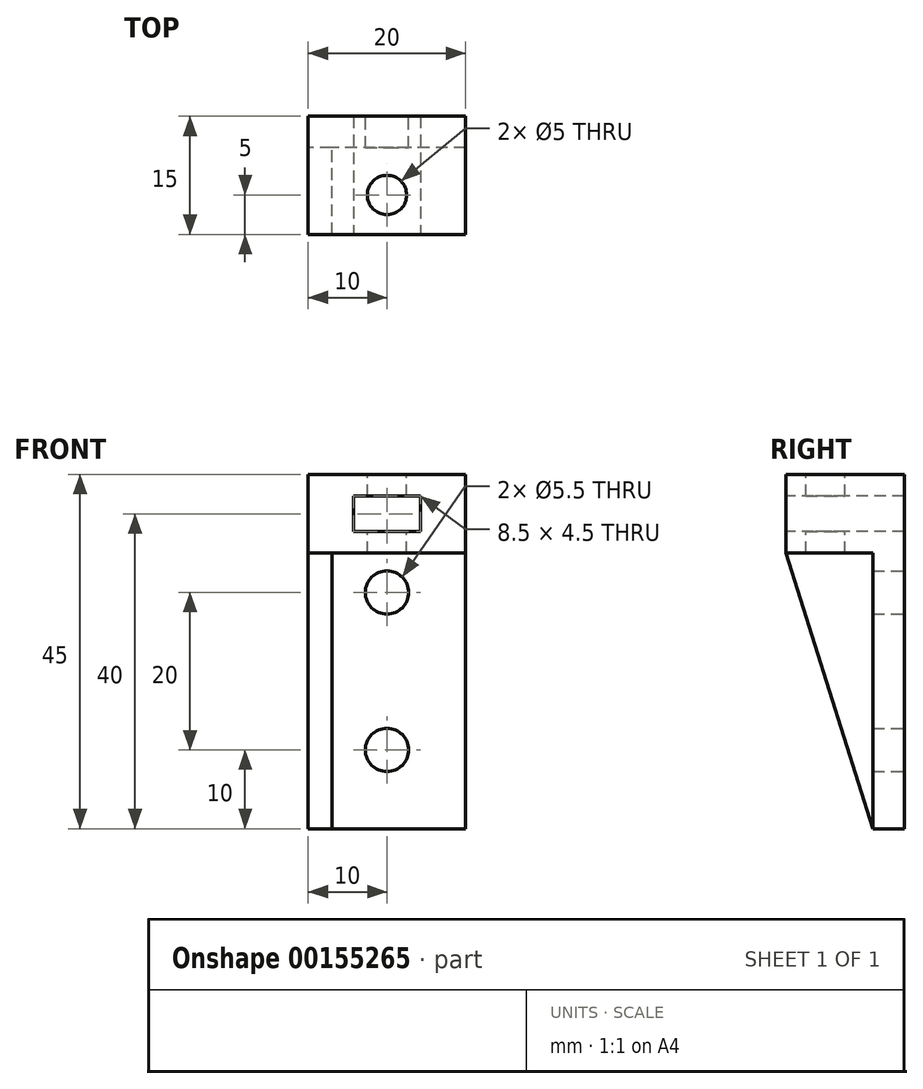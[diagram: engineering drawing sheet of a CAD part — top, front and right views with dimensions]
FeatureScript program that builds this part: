
annotation { "Feature Type Name" : "Feature", "Feature Type Description" : "" }
export const myFeature = defineFeature(function(context is Context, id is Id, definition is map)
    precondition{}
    {
        {
            var Q0;
            Q0=qCreatedBy(makeId("Front.planeOp"),FACE);
            var sketch = newSketch(context, id + "F0", { "sketchPlane" : qUnion([Q0])});
            skCircle(sketch, "E0", {"center": v(0, 10) * mm, "radius": 2.75 * mm});
            skCircle(sketch, "E1", {"center": v(0, -10) * mm, "radius": 2.75 * mm});
            skLineSegment(sketch, "E2.bottom", {"start": v(10, -20) * mm, "end": v(-10, -20) * mm});
            skLineSegment(sketch, "E2.top", {"start": v(10, 20) * mm, "end": v(-10, 20) * mm});
            skLineSegment(sketch, "E2.left", {"start": v(10, -20) * mm, "end": v(10, 20) * mm});
            skLineSegment(sketch, "E2.right", {"start": v(-10, -20) * mm, "end": v(-10, 20) * mm});
            skPoint(sketch, "E2.middle", {"position": v(0, 0) * mm});
            skSolve(sketch);
        }
        {
            var Q0;
            Q0 = qSketchRegion(id + "F0", true);
            extrude(context, id + "F1", {"entities" : qUnion([Q0]), "depth" : 4 * mm});
        }
        {
            var Q0;
            Q0=makeQuery(id+"F1.opExtrude","CAP_FACE",FACE,{"disambiguationData":[OSD([sQuery(id+"F0.wireOp",EDGE,"E0"),sQuery(id+"F0.wireOp",EDGE,"E1"),sQuery(id+"F0.wireOp",EDGE,"E2.bottom"),sQuery(id+"F0.wireOp",EDGE,"E2.top"),sQuery(id+"F0.wireOp",EDGE,"E2.left"),sQuery(id+"F0.wireOp",EDGE,"E2.right")])],"isStart":true});
            var sketch = newSketch(context, id + "F2", { "sketchPlane" : qUnion([Q0])});
            skLineSegment(sketch, "E3.bottom", {"start": v(10, 15) * mm, "end": v(-10, 15) * mm});
            skLineSegment(sketch, "E3.top", {"start": v(10, 25) * mm, "end": v(-10, 25) * mm});
            skLineSegment(sketch, "E3.left", {"start": v(10, 15) * mm, "end": v(10, 25) * mm});
            skLineSegment(sketch, "E3.right", {"start": v(-10, 15) * mm, "end": v(-10, 25) * mm});
            skSolve(sketch);
        }
        {
            var Q0;
            Q0 = qSketchRegion(id + "F2", true);
            extrude(context, id + "F3", {"entities" : qUnion([Q0]), "operationType" : NewBodyOperationType.ADD, "oppositeDirection" : true, "depth" : 15 * mm});
        }
        {
            var Q0;
            Q0=makeQuery(id+"F3.opExtrude","CAP_FACE",FACE,{"disambiguationData":[OSD([sQuery(id+"F2.wireOp",EDGE,"E3.bottom"),sQuery(id+"F2.wireOp",EDGE,"E3.top"),sQuery(id+"F2.wireOp",EDGE,"E3.left"),sQuery(id+"F2.wireOp",EDGE,"E3.right")])],"isStart":false});
            var sketch = newSketch(context, id + "F4", { "sketchPlane" : qUnion([Q0])});
            skLineSegment(sketch, "E4", {"start": v(-10, 20) * mm, "end": v(10, 20) * mm, "construction": true});
            skLineSegment(sketch, "E5.bottom", {"start": v(4.25, 17.75) * mm, "end": v(-4.25, 17.75) * mm});
            skLineSegment(sketch, "E5.top", {"start": v(4.25, 22.25) * mm, "end": v(-4.25, 22.25) * mm});
            skLineSegment(sketch, "E5.left", {"start": v(4.25, 17.75) * mm, "end": v(4.25, 22.25) * mm});
            skLineSegment(sketch, "E5.right", {"start": v(-4.25, 17.75) * mm, "end": v(-4.25, 22.25) * mm});
            skPoint(sketch, "E5.middle", {"position": v(0, 20) * mm});
            skSolve(sketch);
        }
        {
            var Q0;
            Q0 = qSketchRegion(id + "F4", true);
            extrude(context, id + "F5", {"entities" : qUnion([Q0]), "operationType" : NewBodyOperationType.REMOVE, "oppositeDirection" : true, "depth" : 30 * mm});
        }
        {
            var Q0;
            Q0=makeQuery(id+"F3.opExtrude","SWEPT_FACE",FACE,{"disambiguationData":[OSD([sQuery(id+"F2.wireOp",EDGE,"E3.top")])]});
            var sketch = newSketch(context, id + "F6", { "sketchPlane" : qUnion([Q0])});
            skLineSegment(sketch, "E6", {"start": v(0, -15) * mm, "end": v(0, 0) * mm, "construction": true});
            skCircle(sketch, "E7", {"center": v(0, -10) * mm, "radius": 2.5 * mm});
            skSolve(sketch);
        }
        {
            var Q0;
            Q0 = qSketchRegion(id + "F6", true);
            extrude(context, id + "F7", {"entities" : qUnion([Q0]), "operationType" : NewBodyOperationType.REMOVE, "oppositeDirection" : true, "depth" : 20 * mm});
        }
        {
            var Q0;
            Q0=makeQuery(id+"F3.boolean.opBoolean","MERGE",FACE,{"derivedFrom":[makeQuery(id+"F1.opExtrude","SWEPT_FACE",FACE,{"disambiguationData":[OSD([sQuery(id+"F0.wireOp",EDGE,"E2.right")])]}),makeQuery(id+"F3.opExtrude","SWEPT_FACE",FACE,{"disambiguationData":[OSD([sQuery(id+"F2.wireOp",EDGE,"E3.left")])]})]});
            var sketch = newSketch(context, id + "F8", { "sketchPlane" : qUnion([Q0])});
            skLineSegment(sketch, "E8", {"start": v(15, 15) * mm, "end": v(4, 15) * mm});
            skLineSegment(sketch, "E9", {"start": v(4, 15) * mm, "end": v(4, -20) * mm});
            skLineSegment(sketch, "E10", {"start": v(4, -20) * mm, "end": v(15, 15) * mm});
            skSolve(sketch);
        }
        {
            var Q0;
            Q0 = qSketchRegion(id + "F8", true);
            extrude(context, id + "F9", {"entities" : qUnion([Q0]), "operationType" : NewBodyOperationType.ADD, "oppositeDirection" : true, "depth" : 3 * mm});
        }
    });
